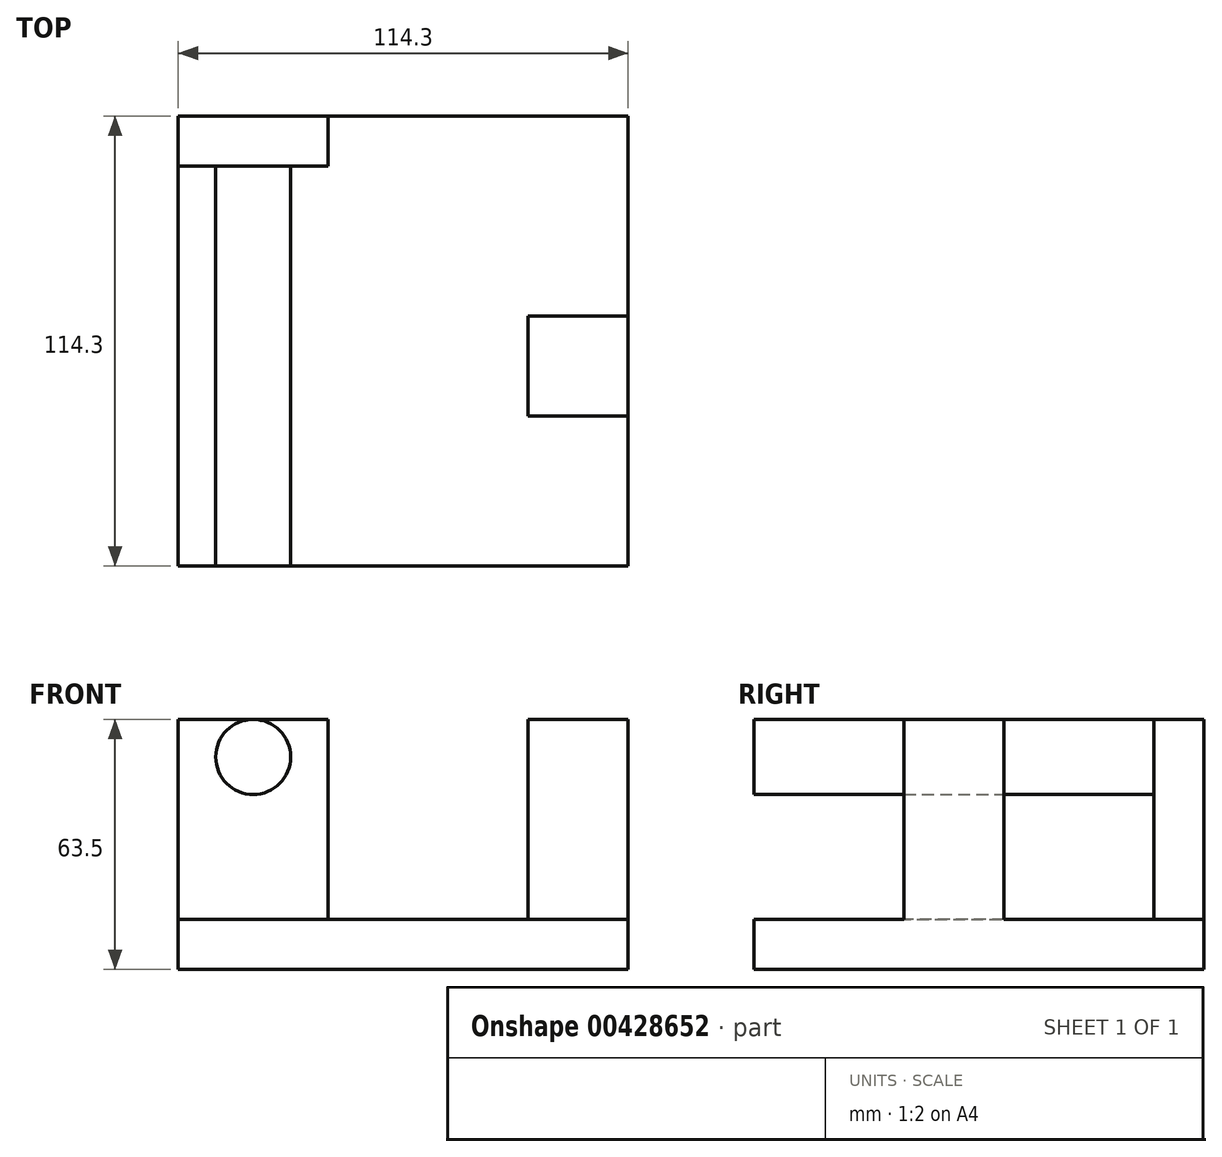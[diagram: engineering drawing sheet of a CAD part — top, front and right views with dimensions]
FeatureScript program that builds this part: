
annotation { "Feature Type Name" : "Feature", "Feature Type Description" : "" }
export const myFeature = defineFeature(function(context is Context, id is Id, definition is map)
    precondition{}
    {
        {
            var Q0;
            Q0=qCreatedBy(makeId("Top.planeOp"),FACE);
            var sketch = newSketch(context, id + "F0", { "sketchPlane" : qUnion([Q0])});
            skLineSegment(sketch, "E0.bottom", {"start": v(114.3, -114.3) * mm, "end": v(0, -114.3) * mm});
            skLineSegment(sketch, "E0.top", {"start": v(114.3, 0) * mm, "end": v(0, 0) * mm});
            skLineSegment(sketch, "E0.left", {"start": v(114.3, -114.3) * mm, "end": v(114.3, 0) * mm});
            skLineSegment(sketch, "E0.right", {"start": v(0, -114.3) * mm, "end": v(0, 0) * mm});
            skSolve(sketch);
        }
        {
            var Q0;
            Q0 = qSketchRegion(id + "F0", true);
            extrude(context, id + "F1", {"entities" : qUnion([Q0]), "depth" : 12.7 * mm});
        }
        {
            var Q0;
            Q0=makeQuery(id+"F1.opExtrude","CAP_FACE",FACE,{"disambiguationData":[OSD([sQuery(id+"F0.wireOp",EDGE,"E0.bottom"),sQuery(id+"F0.wireOp",EDGE,"E0.top"),sQuery(id+"F0.wireOp",EDGE,"E0.left"),sQuery(id+"F0.wireOp",EDGE,"E0.right")])],"isStart":false});
            var sketch = newSketch(context, id + "F2", { "sketchPlane" : qUnion([Q0])});
            skLineSegment(sketch, "E1.bottom", {"start": v(38.1, -12.7) * mm, "end": v(0, -12.7) * mm});
            skLineSegment(sketch, "E1.top", {"start": v(38.1, 0) * mm, "end": v(0, 0) * mm});
            skLineSegment(sketch, "E1.left", {"start": v(38.1, -12.7) * mm, "end": v(38.1, 0) * mm});
            skLineSegment(sketch, "E1.right", {"start": v(0, -12.7) * mm, "end": v(0, 0) * mm});
            skSolve(sketch);
        }
        {
            var Q0;
            Q0 = qSketchRegion(id + "F2", true);
            extrude(context, id + "F3", {"entities" : qUnion([Q0]), "operationType" : NewBodyOperationType.ADD, "depth" : 50.8 * mm});
        }
        {
            var Q0;
            Q0=makeQuery(id+"F3.opExtrude","SWEPT_FACE",FACE,{"disambiguationData":[OSD([sQuery(id+"F2.wireOp",EDGE,"E1.bottom")])]});
            var sketch = newSketch(context, id + "F4", { "sketchPlane" : qUnion([Q0])});
            skCircle(sketch, "E2", {"center": v(19.05, 53.98) * mm, "radius": 9.53 * mm});
            skLineSegment(sketch, "E3", {"start": v(0, 53.98) * mm, "end": v(38.1, 53.98) * mm});
            skSolve(sketch);
        }
        {
            var Q0;
            Q0 = qSketchRegion(id + "F4", true);
            var Q1;
            Q1=makeQuery(id+"F1.opExtrude","SWEPT_FACE",FACE,{"disambiguationData":[OSD([sQuery(id+"F0.wireOp",EDGE,"E0.bottom")])]});
            extrude(context, id + "F5", {"entities" : qUnion([Q0]), "operationType" : NewBodyOperationType.ADD, "endBound" : BoundingType.UP_TO_SURFACE, "endBoundEntityFace" : qUnion([Q1]), "depth" : 25.4 * mm});
        }
        {
            var Q0;
            Q0=makeQuery(id+"F1.opExtrude","CAP_FACE",FACE,{"disambiguationData":[OSD([sQuery(id+"F0.wireOp",EDGE,"E0.bottom"),sQuery(id+"F0.wireOp",EDGE,"E0.top"),sQuery(id+"F0.wireOp",EDGE,"E0.left"),sQuery(id+"F0.wireOp",EDGE,"E0.right")])],"isStart":false});
            var sketch = newSketch(context, id + "F6", { "sketchPlane" : qUnion([Q0])});
            skLineSegment(sketch, "E4.bottom", {"start": v(114.3, -50.8) * mm, "end": v(88.9, -50.8) * mm});
            skLineSegment(sketch, "E4.top", {"start": v(114.3, -76.2) * mm, "end": v(88.9, -76.2) * mm});
            skLineSegment(sketch, "E4.left", {"start": v(114.3, -50.8) * mm, "end": v(114.3, -76.2) * mm});
            skLineSegment(sketch, "E4.right", {"start": v(88.9, -50.8) * mm, "end": v(88.9, -76.2) * mm});
            skLineSegment(sketch, "E5", {"start": v(88.9, -63.5) * mm, "end": v(0, -63.5) * mm});
            skPoint(sketch, "E6.end.orphan", {"position": v(114.3, -142.32) * mm});
            skSolve(sketch);
        }
        {
            var Q0;
            {var subQ1=sQuery(id+"F6.wireOp",EDGE,"E4.bottom");Q0=makeQuery(id+"F6.imprint","IMPRINT",FACE,{"disambiguationData":[TD([[makeQuery(id+"F6.imprint","IMPRINT",EDGE,{"derivedFrom":subQ1}),1.0]])]});}
            var Q1;
            Q1=makeQuery(id+"F3.opExtrude","CAP_FACE",FACE,{"disambiguationData":[OSD([sQuery(id+"F2.wireOp",EDGE,"E1.bottom"),sQuery(id+"F2.wireOp",EDGE,"E1.top"),sQuery(id+"F2.wireOp",EDGE,"E1.left"),sQuery(id+"F2.wireOp",EDGE,"E1.right")])],"isStart":false});
            extrude(context, id + "F7", {"entities" : qUnion([Q0]), "operationType" : NewBodyOperationType.ADD, "endBound" : BoundingType.UP_TO_SURFACE, "endBoundEntityFace" : qUnion([Q1]), "depth" : 25.4 * mm});
        }
    });
